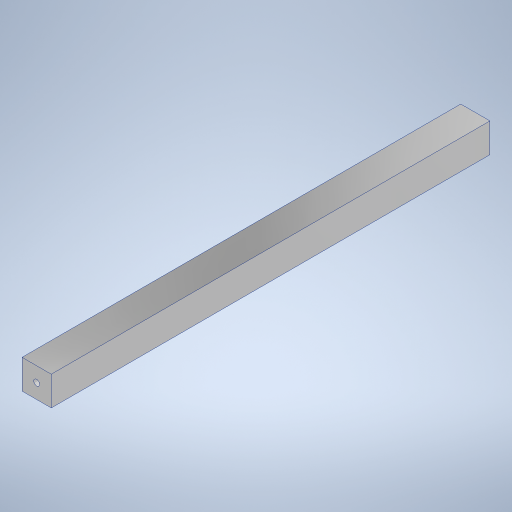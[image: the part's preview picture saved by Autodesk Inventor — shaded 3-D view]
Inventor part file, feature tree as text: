
AUTODESK INVENTOR PART (.ipt)
format: ipt  version: 2024 (Build 280153000, 153)  size: 243,712 bytes
history: native  units: in
note: dims shown in document units (in); Inventor stores cm internally (conversion verified against a paired STEP export)
features: extrude x2, sketch x2
ambient origin geometry x8: Origin, YZ Plane, XZ Plane, XY Plane, X Axis, Y Axis, Z Axis, Center Point
bodies: Solid1 (feature_tree)
feature tree (4):
  extrude  "Extrusion1"  Depth=0.7874in
  extrude  "Extrusion2"  Depth=9.8425in
  sketch  "Sketch1"  dims[d0=0.7874in d1=0.7874in]
  sketch  "Sketch2"  dims[d2=11.811in d3=0.0in d4=0.1575in d5=0.3937in d6=0.3937in d7=9.8425in d8=0.0in]
